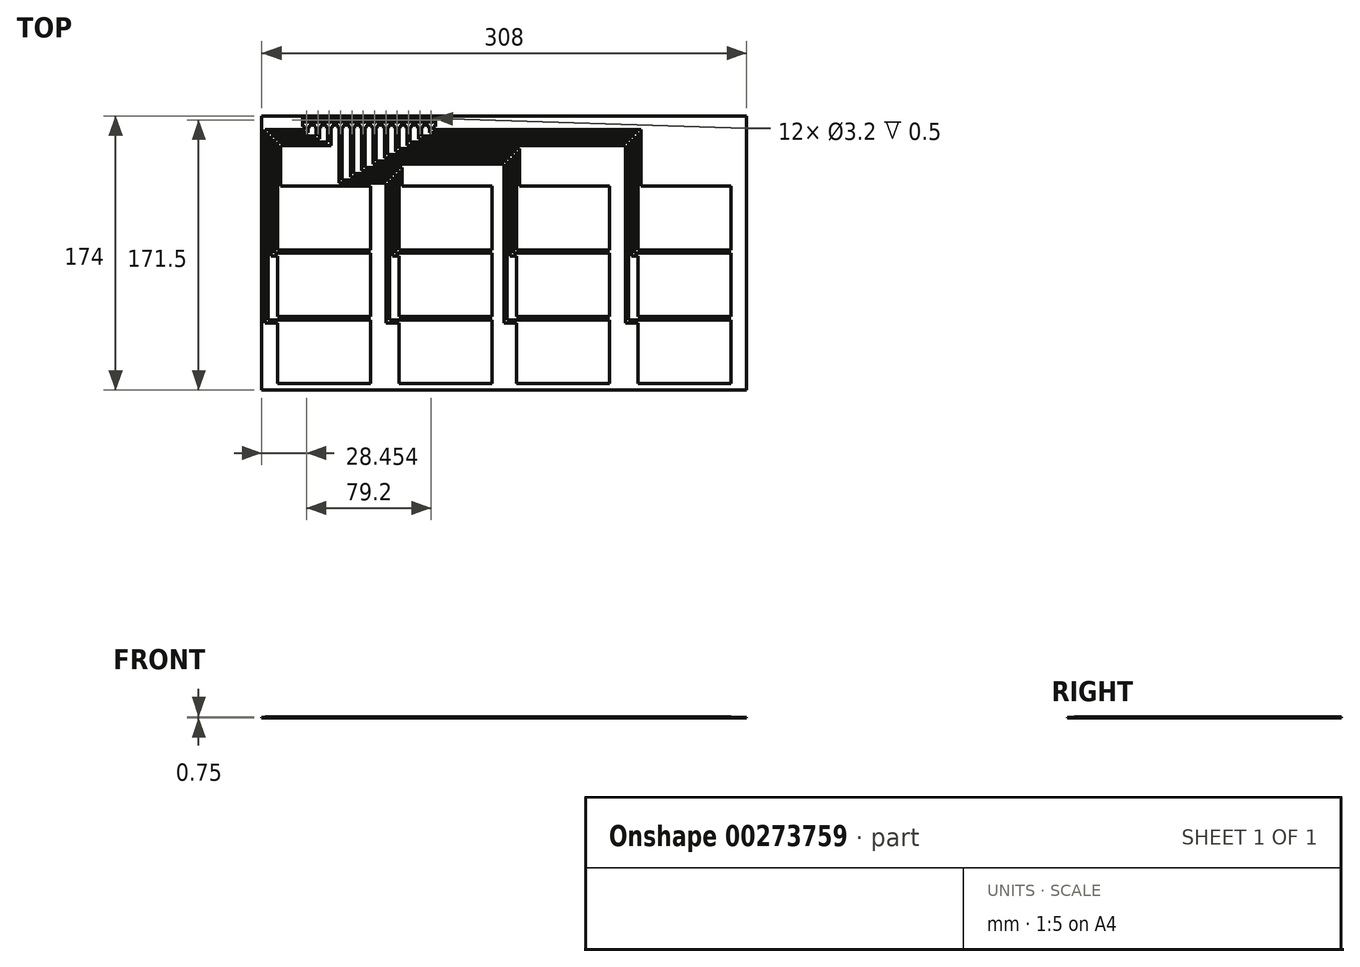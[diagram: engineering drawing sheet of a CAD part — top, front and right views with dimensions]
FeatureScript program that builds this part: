
annotation { "Feature Type Name" : "Feature", "Feature Type Description" : "" }
export const myFeature = defineFeature(function(context is Context, id is Id, definition is map)
    precondition{}
    {
        {
            var Q0;
            Q0=qCreatedBy(makeId("Top.planeOp"),FACE);
            var sketch = newSketch(context, id + "F0", { "sketchPlane" : qUnion([Q0])});
            skLineSegment(sketch, "E0.bottom", {"start": v(154, 87) * mm, "end": v(-154, 87) * mm});
            skLineSegment(sketch, "E0.top", {"start": v(154, -87) * mm, "end": v(-154, -87) * mm});
            skLineSegment(sketch, "E0.left", {"start": v(154, 87) * mm, "end": v(154, -87) * mm});
            skLineSegment(sketch, "E0.right", {"start": v(-154, 87) * mm, "end": v(-154, -87) * mm});
            skPoint(sketch, "E0.middle", {"position": v(0, 0) * mm});
            skSolve(sketch);
        }
        {
            var Q0;
            Q0=makeQuery(id+"F0.imprint","IMPRINT",FACE,{"disambiguationData":[TD([[makeQuery(id+"F0.imprint","IMPRINT",EDGE,{"derivedFrom":sQuery(id+"F0.wireOp",EDGE,"E0.bottom")}),1.0]])]});
            extrude(context, id + "F1", {"entities" : qUnion([Q0]), "depth" : .25 * mm});
        }
        {
            var Q0;
            Q0=makeQuery(id+"F1.opExtrude","CAP_FACE",FACE,{"disambiguationData":[OSD([sQuery(id+"F0.wireOp",EDGE,"E0.bottom"),sQuery(id+"F0.wireOp",EDGE,"E0.top"),sQuery(id+"F0.wireOp",EDGE,"E0.left"),sQuery(id+"F0.wireOp",EDGE,"E0.right")])],"isStart":false});
            var sketch = newSketch(context, id + "F2", { "sketchPlane" : qUnion([Q0])});
            skLineSegment(sketch, "E1", {"start": v(-85.95, 87) * mm, "end": v(-85.95, 80.4) * mm, "construction": true});
            skCircle(sketch, "E2", {"center": v(-89.55, 84.5) * mm, "radius": 1.6 * mm});
            skLineSegment(sketch, "E3", {"start": v(-89.55, 84.5) * mm, "end": v(-89.55, 80.4) * mm, "construction": true});
            skPoint(sketch, "E4", {"position": v(0, 80.62) * mm});
            skLineSegment(sketch, "E5.direction1", {"start": v(-89.55, 84.5) * mm, "end": v(-82.35, 84.5) * mm, "construction": true});
            skLineSegment(sketch, "E6", {"start": v(-86.95, 87) * mm, "end": v(-86.95, 80.4) * mm});
            skLineSegment(sketch, "E7.MirrorCS", {"start": v(-92.15, 87) * mm, "end": v(-92.15, 80.4) * mm});
            skLineSegment(sketch, "E8.trimOffspring", {"start": v(-92.15, 80.4) * mm, "end": v(-86.95, 80.4) * mm});
            skLineSegment(sketch, "E9.trimOffspring", {"start": v(-92.15, 87) * mm, "end": v(-86.95, 87) * mm});
            skCircle(sketch, "E10.1.0.0", {"center": v(-96.75, 84.5) * mm, "radius": 1.6 * mm});
            skLineSegment(sketch, "E10.1.0.1", {"start": v(-99.35, 87) * mm, "end": v(-99.35, 80.4) * mm});
            skLineSegment(sketch, "E10.1.0.2", {"start": v(-99.35, 87) * mm, "end": v(-94.15, 87) * mm});
            skLineSegment(sketch, "E10.1.0.3", {"start": v(-94.15, 87) * mm, "end": v(-94.15, 80.4) * mm});
            skLineSegment(sketch, "E10.1.0.4", {"start": v(-99.35, 80.4) * mm, "end": v(-94.15, 80.4) * mm});
            skCircle(sketch, "E10.2.0.0", {"center": v(-103.95, 84.5) * mm, "radius": 1.6 * mm});
            skLineSegment(sketch, "E10.2.0.1", {"start": v(-106.55, 87) * mm, "end": v(-106.55, 80.4) * mm});
            skLineSegment(sketch, "E10.2.0.2", {"start": v(-106.55, 87) * mm, "end": v(-101.35, 87) * mm});
            skLineSegment(sketch, "E10.2.0.3", {"start": v(-101.35, 87) * mm, "end": v(-101.35, 80.4) * mm});
            skLineSegment(sketch, "E10.2.0.4", {"start": v(-106.55, 80.4) * mm, "end": v(-101.35, 80.4) * mm});
            skCircle(sketch, "E10.3.0.0", {"center": v(-111.15, 84.5) * mm, "radius": 1.6 * mm});
            skLineSegment(sketch, "E10.3.0.1", {"start": v(-113.75, 87) * mm, "end": v(-113.75, 80.4) * mm});
            skLineSegment(sketch, "E10.3.0.2", {"start": v(-113.75, 87) * mm, "end": v(-108.55, 87) * mm});
            skLineSegment(sketch, "E10.3.0.3", {"start": v(-108.55, 87) * mm, "end": v(-108.55, 80.4) * mm});
            skLineSegment(sketch, "E10.3.0.4", {"start": v(-113.75, 80.4) * mm, "end": v(-108.55, 80.4) * mm});
            skCircle(sketch, "E10.4.0.0", {"center": v(-118.35, 84.5) * mm, "radius": 1.6 * mm});
            skLineSegment(sketch, "E10.4.0.1", {"start": v(-120.95, 87) * mm, "end": v(-120.95, 80.4) * mm});
            skLineSegment(sketch, "E10.4.0.2", {"start": v(-120.95, 87) * mm, "end": v(-115.75, 87) * mm});
            skLineSegment(sketch, "E10.4.0.3", {"start": v(-115.75, 87) * mm, "end": v(-115.75, 80.4) * mm});
            skLineSegment(sketch, "E10.4.0.4", {"start": v(-120.95, 80.4) * mm, "end": v(-115.75, 80.4) * mm});
            skCircle(sketch, "E10.5.0.0", {"center": v(-125.55, 84.5) * mm, "radius": 1.6 * mm});
            skLineSegment(sketch, "E10.5.0.1", {"start": v(-128.15, 87) * mm, "end": v(-128.15, 80.4) * mm});
            skLineSegment(sketch, "E10.5.0.2", {"start": v(-128.15, 87) * mm, "end": v(-122.95, 87) * mm});
            skLineSegment(sketch, "E10.5.0.3", {"start": v(-122.95, 87) * mm, "end": v(-122.95, 80.4) * mm});
            skLineSegment(sketch, "E10.5.0.4", {"start": v(-128.15, 80.4) * mm, "end": v(-122.95, 80.4) * mm});
            skLineSegment(sketch, "E10.direction1", {"start": v(-89.55, 84.5) * mm, "end": v(-96.75, 84.5) * mm, "construction": true});
            skCircle(sketch, "E11.MirrorC", {"center": v(-82.35, 84.5) * mm, "radius": 1.6 * mm});
            skLineSegment(sketch, "E12.MirrorCS", {"start": v(-79.75, 80.4) * mm, "end": v(-84.95, 80.4) * mm});
            skLineSegment(sketch, "E13.MirrorCS", {"start": v(-84.95, 87) * mm, "end": v(-84.95, 80.4) * mm});
            skLineSegment(sketch, "E14.MirrorCS", {"start": v(-79.75, 87) * mm, "end": v(-84.95, 87) * mm});
            skLineSegment(sketch, "E15.MirrorCS", {"start": v(-79.75, 87) * mm, "end": v(-79.75, 80.4) * mm});
            skLineSegment(sketch, "E16.MirrorCS", {"start": v(-77.75, 87) * mm, "end": v(-77.75, 80.4) * mm});
            skCircle(sketch, "E17.MirrorC", {"center": v(-75.15, 84.5) * mm, "radius": 1.6 * mm});
            skLineSegment(sketch, "E18.MirrorCS", {"start": v(-72.55, 87) * mm, "end": v(-77.75, 87) * mm});
            skLineSegment(sketch, "E19.MirrorCS", {"start": v(-72.55, 87) * mm, "end": v(-72.55, 80.4) * mm});
            skLineSegment(sketch, "E20.MirrorCS", {"start": v(-70.55, 87) * mm, "end": v(-70.55, 80.4) * mm});
            skCircle(sketch, "E21.MirrorC", {"center": v(-67.95, 84.5) * mm, "radius": 1.6 * mm});
            skLineSegment(sketch, "E22.MirrorCS", {"start": v(-65.35, 87) * mm, "end": v(-65.35, 80.4) * mm});
            skLineSegment(sketch, "E23.MirrorCS", {"start": v(-65.35, 87) * mm, "end": v(-70.55, 87) * mm});
            skLineSegment(sketch, "E24.MirrorCS", {"start": v(-63.35, 87) * mm, "end": v(-63.35, 80.4) * mm});
            skLineSegment(sketch, "E25.MirrorCS", {"start": v(-58.15, 87) * mm, "end": v(-63.35, 87) * mm});
            skCircle(sketch, "E26.MirrorC", {"center": v(-60.75, 84.5) * mm, "radius": 1.6 * mm});
            skLineSegment(sketch, "E27.MirrorCS", {"start": v(-58.15, 87) * mm, "end": v(-58.15, 80.4) * mm});
            skLineSegment(sketch, "E28.MirrorCS", {"start": v(-58.15, 80.4) * mm, "end": v(-63.35, 80.4) * mm});
            skLineSegment(sketch, "E29.MirrorCS", {"start": v(-56.15, 87) * mm, "end": v(-56.15, 80.4) * mm});
            skLineSegment(sketch, "E30.MirrorCS", {"start": v(-50.95, 87) * mm, "end": v(-56.15, 87) * mm});
            skLineSegment(sketch, "E31.MirrorCS", {"start": v(-50.95, 87) * mm, "end": v(-50.95, 80.4) * mm});
            skCircle(sketch, "E32.MirrorC", {"center": v(-53.55, 84.5) * mm, "radius": 1.6 * mm});
            skLineSegment(sketch, "E33.MirrorCS", {"start": v(-48.95, 87) * mm, "end": v(-48.95, 80.4) * mm});
            skCircle(sketch, "E34.MirrorC", {"center": v(-46.35, 84.5) * mm, "radius": 1.6 * mm});
            skLineSegment(sketch, "E35.MirrorCS", {"start": v(-43.75, 87) * mm, "end": v(-48.95, 87) * mm});
            skLineSegment(sketch, "E36.MirrorCS", {"start": v(-43.75, 87) * mm, "end": v(-43.75, 80.4) * mm});
            skLineSegment(sketch, "E37.top", {"start": v(-84.86, 0) * mm, "end": v(-144, 0) * mm});
            skLineSegment(sketch, "E37.left", {"start": v(-84.86, 42.4) * mm, "end": v(-84.86, 2) * mm});
            skLineSegment(sketch, "E38", {"start": v(0, 87) * mm, "end": v(0, -87) * mm, "construction": true});
            skLineSegment(sketch, "E39.bottom", {"start": v(-66.94, 42.4) * mm, "end": v(-7.8, 42.4) * mm});
            skLineSegment(sketch, "E39.top", {"start": v(-66.94, 2) * mm, "end": v(-7.8, 2) * mm});
            skLineSegment(sketch, "E39.left", {"start": v(-66.94, 42.4) * mm, "end": v(-66.94, 2) * mm});
            skLineSegment(sketch, "E39.right", {"start": v(-7.8, 42.4) * mm, "end": v(-7.8, 2) * mm});
            skLineSegment(sketch, "E40.bottom", {"start": v(-144, 2) * mm, "end": v(-84.86, 2) * mm});
            skLineSegment(sketch, "E40.left", {"start": v(-144, 0) * mm, "end": v(-144, -40.4) * mm});
            skLineSegment(sketch, "E41.left", {"start": v(-144, -42.4) * mm, "end": v(-144, -82.8) * mm});
            skLineSegment(sketch, "E41.right", {"start": v(-84.86, -42.4) * mm, "end": v(-84.86, -82.8) * mm});
            skLineSegment(sketch, "E42.bottom", {"start": v(-66.94, 0) * mm, "end": v(-7.8, 0) * mm});
            skLineSegment(sketch, "E42.top", {"start": v(-66.94, -40.4) * mm, "end": v(-7.8, -40.4) * mm});
            skLineSegment(sketch, "E42.left", {"start": v(-66.94, 0) * mm, "end": v(-66.94, -40.4) * mm});
            skLineSegment(sketch, "E42.right", {"start": v(-7.8, 0) * mm, "end": v(-7.8, -40.4) * mm});
            skLineSegment(sketch, "E43.bottom", {"start": v(-66.94, -42.4) * mm, "end": v(-7.8, -42.4) * mm});
            skLineSegment(sketch, "E43.top", {"start": v(-66.94, -82.8) * mm, "end": v(-7.8, -82.8) * mm});
            skLineSegment(sketch, "E43.left", {"start": v(-66.94, -42.4) * mm, "end": v(-66.94, -82.8) * mm});
            skLineSegment(sketch, "E43.right", {"start": v(-7.8, -42.4) * mm, "end": v(-7.8, -82.8) * mm});
            skLineSegment(sketch, "E44", {"start": v(-144, 87) * mm, "end": v(-154, 87) * mm, "construction": true});
            skLineSegment(sketch, "E45", {"start": v(-36.86, -77) * mm, "end": v(-36.86, -87) * mm, "construction": true});
            skLineSegment(sketch, "E46", {"start": v(-144, -40.4) * mm, "end": v(-144, -42.4) * mm, "construction": true});
            skLineSegment(sketch, "E47", {"start": v(-66.94, 2) * mm, "end": v(-66.94, 0) * mm, "construction": true});
            skLineSegment(sketch, "E48", {"start": v(-66.94, -40.4) * mm, "end": v(-66.94, -42.4) * mm, "construction": true});
            skLineSegment(sketch, "E49", {"start": v(-84.86, 0) * mm, "end": v(-84.86, -40.4) * mm});
            skLineSegment(sketch, "E50", {"start": v(-84.86, -40.4) * mm, "end": v(-144, -40.4) * mm});
            skLineSegment(sketch, "E51", {"start": v(-144, -42.4) * mm, "end": v(-84.86, -42.4) * mm});
            skLineSegment(sketch, "E52", {"start": v(-84.86, 42.4) * mm, "end": v(-66.94, 42.4) * mm, "construction": true});
            skLineSegment(sketch, "E53", {"start": v(-124.55, 80.4) * mm, "end": v(-124.55, 76.4) * mm});
            skLineSegment(sketch, "E54", {"start": v(-124.55, 76.4) * mm, "end": v(-150, 76.4) * mm});
            skLineSegment(sketch, "E55", {"start": v(-150, 76.4) * mm, "end": v(-150, -42.4) * mm});
            skPoint(sketch, "E56", {"position": v(-125.55, 80.4) * mm});
            skPoint(sketch, "E57", {"position": v(-118.35, 80.4) * mm});
            skPoint(sketch, "E58", {"position": v(-111.15, 80.4) * mm});
            skLineSegment(sketch, "E59", {"start": v(-117.35, 80.4) * mm, "end": v(-117.35, 72.4) * mm});
            skLineSegment(sketch, "E60", {"start": v(-117.35, 72.4) * mm, "end": v(-146, 72.4) * mm});
            skLineSegment(sketch, "E61", {"start": v(-146, 72.4) * mm, "end": v(-146, 0) * mm});
            skLineSegment(sketch, "E62", {"start": v(-110.15, 80.4) * mm, "end": v(-110.15, 68.4) * mm});
            skLineSegment(sketch, "E63", {"start": v(-146, 0) * mm, "end": v(-144, 0) * mm});
            skLineSegment(sketch, "E64", {"start": v(-144, -42.4) * mm, "end": v(-150, -42.4) * mm});
            skLineSegment(sketch, "E65.0", {"start": v(-148, -2) * mm, "end": v(-144, -2) * mm});
            skLineSegment(sketch, "E65.1", {"start": v(-148, 74.4) * mm, "end": v(-148, -2) * mm});
            skLineSegment(sketch, "E65.2", {"start": v(-119.35, 74.4) * mm, "end": v(-148, 74.4) * mm});
            skLineSegment(sketch, "E65.3", {"start": v(-119.35, 80.4) * mm, "end": v(-119.35, 74.4) * mm});
            skLineSegment(sketch, "E66.0", {"start": v(-144, -44.4) * mm, "end": v(-152, -44.4) * mm});
            skLineSegment(sketch, "E66.1", {"start": v(-152, 78.4) * mm, "end": v(-152, -44.4) * mm});
            skLineSegment(sketch, "E66.2", {"start": v(-126.55, 78.4) * mm, "end": v(-152, 78.4) * mm});
            skLineSegment(sketch, "E66.3", {"start": v(-126.55, 80.4) * mm, "end": v(-126.55, 78.4) * mm});
            skPoint(sketch, "E67", {"position": v(-103.95, 80.4) * mm});
            skPoint(sketch, "E68", {"position": v(-96.75, 80.4) * mm});
            skPoint(sketch, "E69", {"position": v(-82.35, 80.4) * mm});
            skPoint(sketch, "E70", {"position": v(-75.15, 80.4) * mm});
            skLineSegment(sketch, "E71", {"start": v(-102.95, 80.4) * mm, "end": v(-102.95, 46.4) * mm});
            skLineSegment(sketch, "E72", {"start": v(-102.95, 46.4) * mm, "end": v(-72.94, 46.4) * mm});
            skLineSegment(sketch, "E73", {"start": v(-72.94, 46.4) * mm, "end": v(-72.94, -42.4) * mm});
            skLineSegment(sketch, "E74", {"start": v(-72.94, -42.4) * mm, "end": v(-66.94, -42.4) * mm});
            skLineSegment(sketch, "E75", {"start": v(-95.75, 80.4) * mm, "end": v(-95.75, 50.4) * mm});
            skLineSegment(sketch, "E76", {"start": v(-95.75, 50.4) * mm, "end": v(-68.94, 50.4) * mm});
            skLineSegment(sketch, "E77", {"start": v(-68.94, 50.4) * mm, "end": v(-68.94, 0) * mm});
            skLineSegment(sketch, "E78", {"start": v(-68.94, 0) * mm, "end": v(-66.94, 0) * mm});
            skLineSegment(sketch, "E79.0", {"start": v(-74.94, -44.4) * mm, "end": v(-66.94, -44.4) * mm});
            skLineSegment(sketch, "E79.1", {"start": v(-74.94, 44.4) * mm, "end": v(-74.94, -44.4) * mm});
            skLineSegment(sketch, "E79.2", {"start": v(-104.95, 44.4) * mm, "end": v(-74.94, 44.4) * mm});
            skLineSegment(sketch, "E79.3", {"start": v(-104.95, 80.4) * mm, "end": v(-104.95, 44.4) * mm});
            skLineSegment(sketch, "E80.0", {"start": v(-70.94, -2) * mm, "end": v(-66.94, -2) * mm});
            skLineSegment(sketch, "E80.1", {"start": v(-70.94, 48.4) * mm, "end": v(-70.94, -2) * mm});
            skLineSegment(sketch, "E80.2", {"start": v(-97.75, 48.4) * mm, "end": v(-70.94, 48.4) * mm});
            skLineSegment(sketch, "E80.3", {"start": v(-97.75, 80.4) * mm, "end": v(-97.75, 48.4) * mm});
            skLineSegment(sketch, "E81", {"start": v(-84.86, -42.4) * mm, "end": v(-72.94, -42.4) * mm, "construction": true});
            skLineSegment(sketch, "E82", {"start": v(-84.86, 0) * mm, "end": v(-68.94, 0) * mm, "construction": true});
            skLineSegment(sketch, "E83", {"start": v(-88.55, 80.4) * mm, "end": v(-88.55, 54.4) * mm});
            skLineSegment(sketch, "E84", {"start": v(-88.55, 54.4) * mm, "end": v(-64.94, 54.4) * mm});
            skLineSegment(sketch, "E85", {"start": v(-64.94, 54.4) * mm, "end": v(-64.94, 42.4) * mm});
            skLineSegment(sketch, "E86", {"start": v(-81.35, 80.4) * mm, "end": v(-81.35, 58.4) * mm});
            skLineSegment(sketch, "E87", {"start": v(-144, 42.4) * mm, "end": v(-144, 2) * mm});
            skLineSegment(sketch, "E88", {"start": v(-144, 2) * mm, "end": v(-144, 0) * mm, "construction": true});
            skLineSegment(sketch, "E89.MirrorCS", {"start": v(7.8, 42.4) * mm, "end": v(7.8, 2) * mm});
            skLineSegment(sketch, "E90.MirrorCS", {"start": v(66.94, 42.4) * mm, "end": v(7.8, 42.4) * mm});
            skLineSegment(sketch, "E91.MirrorCS", {"start": v(66.94, 42.4) * mm, "end": v(66.94, 2) * mm});
            skLineSegment(sketch, "E92.MirrorCS", {"start": v(66.94, 2) * mm, "end": v(7.8, 2) * mm});
            skLineSegment(sketch, "E93.MirrorCS", {"start": v(84.86, 42.4) * mm, "end": v(84.86, 2) * mm});
            skLineSegment(sketch, "E94.MirrorCS", {"start": v(84.86, 42.4) * mm, "end": v(144, 42.4) * mm});
            skLineSegment(sketch, "E95.MirrorCS", {"start": v(144, 42.4) * mm, "end": v(144, 2) * mm});
            skLineSegment(sketch, "E96.MirrorCS", {"start": v(144, 2) * mm, "end": v(84.86, 2) * mm});
            skLineSegment(sketch, "E97.MirrorCS", {"start": v(84.86, 0) * mm, "end": v(144, 0) * mm});
            skLineSegment(sketch, "E98.MirrorCS", {"start": v(144, 0) * mm, "end": v(144, -40.4) * mm});
            skLineSegment(sketch, "E99.MirrorCS", {"start": v(84.86, 0) * mm, "end": v(84.86, -40.4) * mm});
            skLineSegment(sketch, "E100.MirrorCS", {"start": v(144, -42.4) * mm, "end": v(84.86, -42.4) * mm});
            skLineSegment(sketch, "E101.MirrorCS", {"start": v(84.86, -42.4) * mm, "end": v(84.86, -82.8) * mm});
            skLineSegment(sketch, "E102.MirrorCS", {"start": v(66.94, -42.4) * mm, "end": v(66.94, -82.8) * mm});
            skLineSegment(sketch, "E103.MirrorCS", {"start": v(7.8, -42.4) * mm, "end": v(7.8, -82.8) * mm});
            skLineSegment(sketch, "E104.MirrorCS", {"start": v(66.94, -42.4) * mm, "end": v(7.8, -42.4) * mm});
            skLineSegment(sketch, "E105.MirrorCS", {"start": v(66.94, -40.4) * mm, "end": v(7.8, -40.4) * mm});
            skLineSegment(sketch, "E106.MirrorCS", {"start": v(7.8, 0) * mm, "end": v(7.8, -40.4) * mm});
            skLineSegment(sketch, "E107.MirrorCS", {"start": v(66.94, 0) * mm, "end": v(66.94, -40.4) * mm});
            skLineSegment(sketch, "E108.MirrorCS", {"start": v(66.94, 0) * mm, "end": v(7.8, 0) * mm});
            skLineSegment(sketch, "E109.MirrorCS", {"start": v(84.86, -40.4) * mm, "end": v(144, -40.4) * mm});
            skLineSegment(sketch, "E110", {"start": v(7.8, -82.8) * mm, "end": v(66.94, -82.8) * mm});
            skLineSegment(sketch, "E111", {"start": v(1.8, 58.4) * mm, "end": v(1.8, -42.4) * mm});
            skLineSegment(sketch, "E112", {"start": v(-81.35, 58.4) * mm, "end": v(1.8, 58.4) * mm});
            skLineSegment(sketch, "E113", {"start": v(7.8, -42.4) * mm, "end": v(1.8, -42.4) * mm});
            skLineSegment(sketch, "E114.0", {"start": v(-66.94, 52.4) * mm, "end": v(-66.94, 42.4) * mm});
            skLineSegment(sketch, "E114.1", {"start": v(-90.55, 52.4) * mm, "end": v(-66.94, 52.4) * mm});
            skLineSegment(sketch, "E114.2", {"start": v(-90.55, 80.4) * mm, "end": v(-90.55, 52.4) * mm});
            skLineSegment(sketch, "E115.0", {"start": v(7.8, -44.4) * mm, "end": v(-0.2, -44.4) * mm});
            skLineSegment(sketch, "E115.1", {"start": v(-0.2, 56.4) * mm, "end": v(-0.2, -44.4) * mm});
            skLineSegment(sketch, "E115.2", {"start": v(-83.35, 56.4) * mm, "end": v(-0.2, 56.4) * mm});
            skLineSegment(sketch, "E115.3", {"start": v(-83.35, 80.4) * mm, "end": v(-83.35, 56.4) * mm});
            skLineSegment(sketch, "E116", {"start": v(-74.15, 80.4) * mm, "end": v(-74.15, 62.4) * mm});
            skLineSegment(sketch, "E117", {"start": v(-74.15, 62.4) * mm, "end": v(5.8, 62.4) * mm});
            skLineSegment(sketch, "E118", {"start": v(5.8, 62.4) * mm, "end": v(5.8, 0) * mm});
            skLineSegment(sketch, "E119", {"start": v(5.8, 0) * mm, "end": v(7.8, 0) * mm});
            skLineSegment(sketch, "E120.0", {"start": v(3.8, -2) * mm, "end": v(7.8, -2) * mm});
            skLineSegment(sketch, "E120.1", {"start": v(3.8, 60.4) * mm, "end": v(3.8, -2) * mm});
            skLineSegment(sketch, "E120.2", {"start": v(-76.15, 60.4) * mm, "end": v(3.8, 60.4) * mm});
            skLineSegment(sketch, "E120.3", {"start": v(-76.15, 80.4) * mm, "end": v(-76.15, 60.4) * mm});
            skLineSegment(sketch, "E121", {"start": v(-66.95, 80.4) * mm, "end": v(-66.95, 66.4) * mm});
            skLineSegment(sketch, "E122", {"start": v(-66.95, 66.4) * mm, "end": v(9.8, 66.4) * mm});
            skLineSegment(sketch, "E123", {"start": v(9.8, 66.4) * mm, "end": v(9.8, 42.4) * mm});
            skLineSegment(sketch, "E124.0", {"start": v(7.8, 64.4) * mm, "end": v(7.8, 42.4) * mm});
            skLineSegment(sketch, "E124.1", {"start": v(-68.95, 64.4) * mm, "end": v(7.8, 64.4) * mm});
            skLineSegment(sketch, "E124.2", {"start": v(-68.95, 80.4) * mm, "end": v(-68.95, 64.4) * mm});
            skLineSegment(sketch, "E125", {"start": v(-59.75, 80.4) * mm, "end": v(-59.75, 70.4) * mm});
            skLineSegment(sketch, "E126", {"start": v(-59.75, 70.4) * mm, "end": v(78.86, 70.4) * mm});
            skLineSegment(sketch, "E127", {"start": v(78.86, 70.4) * mm, "end": v(78.86, -42.4) * mm});
            skLineSegment(sketch, "E128", {"start": v(78.86, -42.4) * mm, "end": v(84.86, -42.4) * mm});
            skLineSegment(sketch, "E129.2", {"start": v(-61.75, 68.4) * mm, "end": v(76.86, 68.4) * mm});
            skLineSegment(sketch, "E129.3", {"start": v(-61.75, 80.4) * mm, "end": v(-61.75, 68.4) * mm});
            skLineSegment(sketch, "E130", {"start": v(82.86, 74.4) * mm, "end": v(82.86, 0) * mm});
            skLineSegment(sketch, "E131", {"start": v(82.86, 0) * mm, "end": v(84.86, 0) * mm});
            skLineSegment(sketch, "E132.0", {"start": v(80.86, -2) * mm, "end": v(84.86, -2) * mm});
            skLineSegment(sketch, "E132.1", {"start": v(80.86, 72.4) * mm, "end": v(80.86, -2) * mm});
            skLineSegment(sketch, "E132.2", {"start": v(-54.55, 72.4) * mm, "end": v(80.86, 72.4) * mm});
            skLineSegment(sketch, "E132.3", {"start": v(-54.55, 80.4) * mm, "end": v(-54.55, 72.4) * mm});
            skLineSegment(sketch, "E133", {"start": v(-45.35, 80.4) * mm, "end": v(-45.35, 78.4) * mm});
            skLineSegment(sketch, "E134", {"start": v(-45.35, 78.4) * mm, "end": v(86.86, 78.4) * mm});
            skLineSegment(sketch, "E135", {"start": v(86.86, 78.4) * mm, "end": v(86.86, 42.4) * mm});
            skLineSegment(sketch, "E136.0", {"start": v(84.86, 76.4) * mm, "end": v(84.86, 42.4) * mm});
            skLineSegment(sketch, "E136.1", {"start": v(-47.35, 76.4) * mm, "end": v(84.86, 76.4) * mm});
            skLineSegment(sketch, "E137", {"start": v(-144, 42.4) * mm, "end": v(-84.86, 42.4) * mm});
            skLineSegment(sketch, "E138", {"start": v(-112.15, 80.4) * mm, "end": v(-112.15, 70.4) * mm});
            skLineSegment(sketch, "E139", {"start": v(-112.15, 70.4) * mm, "end": v(-144, 70.4) * mm});
            skLineSegment(sketch, "E140", {"start": v(-144, 70.4) * mm, "end": v(-144, 42.4) * mm});
            skLineSegment(sketch, "E141.0", {"start": v(-142, 68.4) * mm, "end": v(-142, 42.4) * mm});
            skLineSegment(sketch, "E141.1", {"start": v(-110.15, 68.4) * mm, "end": v(-142, 68.4) * mm});
            skLineSegment(sketch, "E142", {"start": v(76.86, 68.4) * mm, "end": v(76.86, -44.4) * mm});
            skLineSegment(sketch, "E143", {"start": v(76.86, -44.4) * mm, "end": v(84.86, -44.4) * mm});
            skLineSegment(sketch, "E144", {"start": v(-56.15, 80.4) * mm, "end": v(-50.95, 80.4) * mm});
            skPoint(sketch, "E145", {"position": v(-53.55, 80.4) * mm});
            skLineSegment(sketch, "E146", {"start": v(-70.55, 80.4) * mm, "end": v(-65.35, 80.4) * mm});
            skPoint(sketch, "E147", {"position": v(-67.95, 80.4) * mm});
            skLineSegment(sketch, "E148", {"start": v(-67.95, 84.5) * mm, "end": v(-67.95, 80.4) * mm, "construction": true});
            skLineSegment(sketch, "E149", {"start": v(-60.75, 84.5) * mm, "end": v(-60.75, 80.4) * mm, "construction": true});
            skLineSegment(sketch, "E150", {"start": v(-52.55, 80.4) * mm, "end": v(-52.55, 74.4) * mm});
            skLineSegment(sketch, "E151", {"start": v(-52.55, 74.4) * mm, "end": v(82.86, 74.4) * mm});
            skLineSegment(sketch, "E152", {"start": v(-47.35, 80.4) * mm, "end": v(-47.35, 76.4) * mm});
            skLineSegment(sketch, "E153", {"start": v(-77.75, 80.4) * mm, "end": v(-72.55, 80.4) * mm});
            skLineSegment(sketch, "E154", {"start": v(-48.95, 80.4) * mm, "end": v(-43.75, 80.4) * mm});
            skLineSegment(sketch, "E155", {"start": v(-46.35, 84.5) * mm, "end": v(-46.35, 80.4) * mm, "construction": true});
            skLineSegment(sketch, "E156", {"start": v(-144, -82.8) * mm, "end": v(-84.86, -82.8) * mm});
            skLineSegment(sketch, "E157", {"start": v(84.86, -82.8) * mm, "end": v(144.1, -82.8) * mm});
            skPoint(sketch, "E158.MirrorCS.start.orphan", {"position": v(144, -42.4) * mm});
            skLineSegment(sketch, "E159", {"start": v(144, -42.4) * mm, "end": v(144.1, -82.8) * mm});
            skSolve(sketch);
        }
        {
            var Q0;
            Q0=qSketchRegion(id+"F2",true);
            extrude(context, id + "F3", {"entities" : qUnion([Q0]), "operationType" : NewBodyOperationType.ADD, "depth" : .5 * mm});
        }
    });
